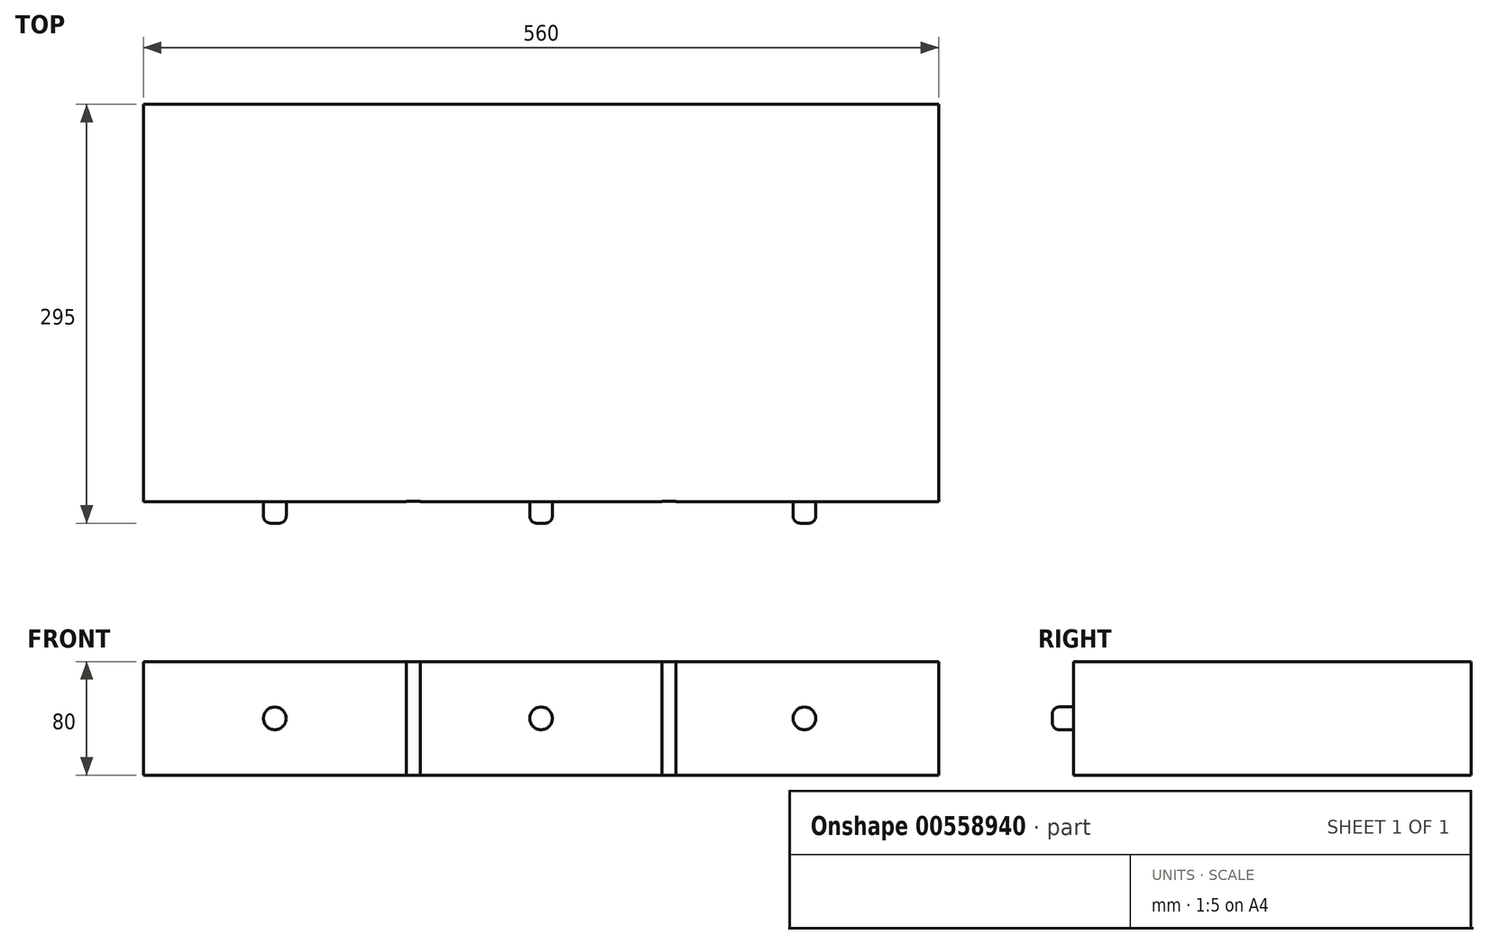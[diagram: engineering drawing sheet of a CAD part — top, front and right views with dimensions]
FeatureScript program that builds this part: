
annotation { "Feature Type Name" : "Feature", "Feature Type Description" : "" }
export const myFeature = defineFeature(function(context is Context, id is Id, definition is map)
    precondition{}
    {
        {
            var Q0;
            Q0=qCreatedBy(makeId("Front.planeOp"),FACE);
            var sketch = newSketch(context, id + "F0", { "sketchPlane" : qUnion([Q0])});
            skLineSegment(sketch, "E0.bottom", {"start": v(280, -40) * mm, "end": v(-280, -40) * mm});
            skLineSegment(sketch, "E0.top", {"start": v(280, 40) * mm, "end": v(-280, 40) * mm});
            skLineSegment(sketch, "E0.left", {"start": v(280, -40) * mm, "end": v(280, 40) * mm});
            skLineSegment(sketch, "E0.right", {"start": v(-280, -40) * mm, "end": v(-280, 40) * mm});
            skPoint(sketch, "E0.middle", {"position": v(0, 0) * mm});
            skSolve(sketch);
        }
        {
            var Q0;
            Q0=makeQuery(id+"F0.imprint","IMPRINT",FACE,{"disambiguationData":[TD([[makeQuery(id+"F0.imprint","IMPRINT",EDGE,{"derivedFrom":sQuery(id+"F0.wireOp",EDGE,"E0.bottom")}),-1.0]])]});
            extrude(context, id + "F1", {"entities" : qUnion([Q0]), "depth" : 280 * mm, "offsetDistance" : 25 * mm});
        }
        {
            var Q0;
            Q0=makeQuery(id+"F1.opExtrude","CAP_FACE",FACE,{"disambiguationData":[OSD([sQuery(id+"F0.wireOp",EDGE,"E0.bottom"),sQuery(id+"F0.wireOp",EDGE,"E0.top"),sQuery(id+"F0.wireOp",EDGE,"E0.left"),sQuery(id+"F0.wireOp",EDGE,"E0.right")])],"isStart":false});
            var sketch = newSketch(context, id + "F2", { "sketchPlane" : qUnion([Q0])});
            skLineSegment(sketch, "E1.bottom", {"start": v(-85, 40) * mm, "end": v(-95, 40) * mm});
            skLineSegment(sketch, "E1.top", {"start": v(-85, -40) * mm, "end": v(-95, -40) * mm});
            skLineSegment(sketch, "E1.left", {"start": v(-85, 40) * mm, "end": v(-85, -40) * mm});
            skLineSegment(sketch, "E1.right", {"start": v(-95, 40) * mm, "end": v(-95, -40) * mm});
            skPoint(sketch, "E1.middle", {"position": v(-90, 0) * mm});
            skLineSegment(sketch, "E2.bottom", {"start": v(95, -40) * mm, "end": v(85, -40) * mm});
            skLineSegment(sketch, "E2.top", {"start": v(95, 40) * mm, "end": v(85, 40) * mm});
            skLineSegment(sketch, "E2.left", {"start": v(95, -40) * mm, "end": v(95, 40) * mm});
            skLineSegment(sketch, "E2.right", {"start": v(85, -40) * mm, "end": v(85, 40) * mm});
            skPoint(sketch, "E2.middle", {"position": v(90, 0) * mm});
            skSolve(sketch);
        }
        {
            var Q0;
            Q0 = qSketchRegion(id + "F2", true);
            extrude(context, id + "F3", {"entities" : qUnion([Q0]), "operationType" : NewBodyOperationType.REMOVE, "oppositeDirection" : true, "depth" : 0.5 * mm, "offsetDistance" : 25 * mm});
        }
        {
            var Q0;
            {var subQ0=sQuery(id+"F0.wireOp",EDGE,"E0.bottom");var subQ1=sQuery(id+"F0.wireOp",EDGE,"E0.right");var subQ2=sQuery(id+"F0.wireOp",EDGE,"E0.top");Q0=makeQuery(id+"F3.boolean.opBoolean","SPLIT",FACE,{"disambiguationData":[TD([makeQuery(id+"F1.opExtrude","SWEPT_FACE",FACE,{"disambiguationData":[OSD([subQ1])]})])],"derivedFrom":makeQuery(id+"F1.opExtrude","CAP_FACE",FACE,{"disambiguationData":[OSD([subQ0,subQ2,sQuery(id+"F0.wireOp",EDGE,"E0.left"),subQ1])],"isStart":false})});}
            var sketch = newSketch(context, id + "F4", { "sketchPlane" : qUnion([Q0])});
            skCircle(sketch, "E3", {"center": v(-187.5, 0) * mm, "radius": 8 * mm});
            skPoint(sketch, "E3.centerSnap0", {"position": v(-95, 0) * mm});
            skPoint(sketch, "E3.centerSnap1", {"position": v(-187.5, 40) * mm});
            skCircle(sketch, "E4", {"center": v(0, 0) * mm, "radius": 8 * mm});
            skCircle(sketch, "E5", {"center": v(185.5, 0) * mm, "radius": 8 * mm});
            skSolve(sketch);
        }
        {
            var Q0;
            Q0 = qSketchRegion(id + "F4", true);
            extrude(context, id + "F5", {"entities" : qUnion([Q0]), "operationType" : NewBodyOperationType.ADD, "depth" : 15 * mm, "offsetDistance" : 25 * mm});
        }
        {
            var Q0;
            Q0=makeQuery(id+"F5.opExtrude","CAP_EDGE",EDGE,{"disambiguationData":[OSD([sQuery(id+"F4.wireOp",EDGE,"E3")])],"isStart":false});
            var Q1;
            Q1=makeQuery(id+"F5.opExtrude","CAP_EDGE",EDGE,{"disambiguationData":[OSD([sQuery(id+"F4.wireOp",EDGE,"E4")])],"isStart":false});
            var Q2;
            Q2=makeQuery(id+"F5.opExtrude","CAP_EDGE",EDGE,{"disambiguationData":[OSD([sQuery(id+"F4.wireOp",EDGE,"E5")])],"isStart":false});
            fillet(context, id + "F6", {"entities" : qUnion([Q0, Q1, Q2]), "radius" : 5 * mm, "tangentPropagation" : true, "allowEdgeOverflow" : false});
        }
    });
